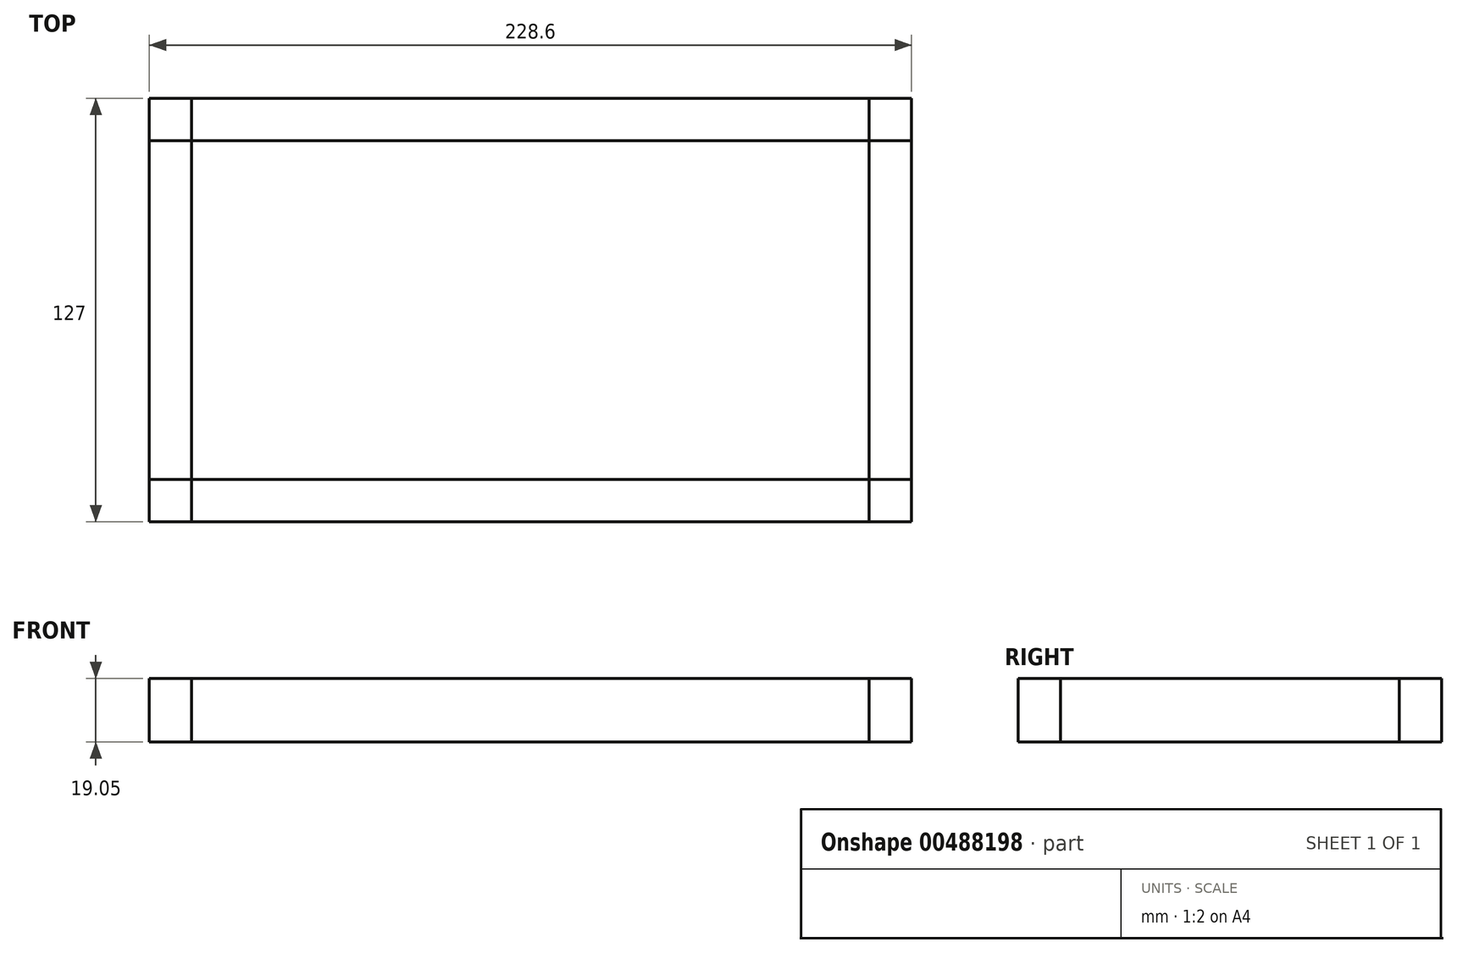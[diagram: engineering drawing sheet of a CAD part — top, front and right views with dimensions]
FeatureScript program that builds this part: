
annotation { "Feature Type Name" : "Feature", "Feature Type Description" : "" }
export const myFeature = defineFeature(function(context is Context, id is Id, definition is map)
    precondition{}
    {
        {
            var Q0;
            Q0=qCreatedBy(makeId("Top.planeOp"),FACE);
            var sketch = newSketch(context, id + "F0", { "sketchPlane" : qUnion([Q0])});
            skLineSegment(sketch, "E0.bottom", {"start": v(101.6, -50.8) * mm, "end": v(-101.6, -50.8) * mm});
            skLineSegment(sketch, "E0.top", {"start": v(101.6, 50.8) * mm, "end": v(-101.6, 50.8) * mm});
            skLineSegment(sketch, "E0.left", {"start": v(101.6, -50.8) * mm, "end": v(101.6, 50.8) * mm});
            skLineSegment(sketch, "E0.right", {"start": v(-101.6, -50.8) * mm, "end": v(-101.6, 50.8) * mm});
            skPoint(sketch, "E0.middle", {"position": v(0, 0) * mm});
            skSolve(sketch);
        }
        {
            var Q0;
            Q0=makeQuery(id+"F0.imprint","IMPRINT",FACE,{"disambiguationData":[TD([[makeQuery(id+"F0.imprint","IMPRINT",EDGE,{"derivedFrom":sQuery(id+"F0.wireOp",EDGE,"E0.bottom")}),-1.0]])]});
            extrude(context, id + "F1", {"entities" : qUnion([Q0]), "depth" : 19.05 * mm});
        }
        {
            var Q0;
            Q0=makeQuery(id+"F1.opExtrude","CAP_FACE",FACE,{"disambiguationData":[OSD([sQuery(id+"F0.wireOp",EDGE,"E0.bottom"),sQuery(id+"F0.wireOp",EDGE,"E0.top"),sQuery(id+"F0.wireOp",EDGE,"E0.left"),sQuery(id+"F0.wireOp",EDGE,"E0.right")])],"isStart":false});
            var sketch = newSketch(context, id + "F2", { "sketchPlane" : qUnion([Q0])});
            skLineSegment(sketch, "E1.bottom", {"start": v(-101.6, -50.8) * mm, "end": v(-114.3, -50.8) * mm});
            skLineSegment(sketch, "E1.top", {"start": v(-101.6, -63.5) * mm, "end": v(-114.3, -63.5) * mm});
            skLineSegment(sketch, "E1.left", {"start": v(-101.6, -50.8) * mm, "end": v(-101.6, -63.5) * mm});
            skLineSegment(sketch, "E1.right", {"start": v(-114.3, -50.8) * mm, "end": v(-114.3, -63.5) * mm});
            skSolve(sketch);
        }
        {
            var Q0;
            Q0=makeQuery(id+"F2.imprint","IMPRINT",FACE,{"disambiguationData":[TD([[makeQuery(id+"F2.imprint","IMPRINT",EDGE,{"derivedFrom":sQuery(id+"F2.wireOp",EDGE,"E1.bottom")}),1.0]])]});
            extrude(context, id + "F3", {"entities" : qUnion([Q0]), "oppositeDirection" : true, "depth" : 19.05 * mm});
        }
        {
            var Q0;
            Q0=makeQuery(id+"F3.opExtrude","SWEPT_BODY",BODY,{"disambiguationData":[OSD([sQuery(id+"F2.wireOp",EDGE,"E1.bottom"),sQuery(id+"F2.wireOp",EDGE,"E1.top"),sQuery(id+"F2.wireOp",EDGE,"E1.left"),sQuery(id+"F2.wireOp",EDGE,"E1.right")])]});
            var Q1;
            Q1=qCreatedBy(makeId("Right.planeOp"),FACE);
            mirror(context, id + "F4", {"entities" : qUnion([Q0]), "mirrorPlane" : qUnion([Q1])});
        }
        {
            var Q0;
            Q0=makeQuery(id+"F3.opExtrude","SWEPT_BODY",BODY,{"disambiguationData":[OSD([sQuery(id+"F2.wireOp",EDGE,"E1.bottom"),sQuery(id+"F2.wireOp",EDGE,"E1.top"),sQuery(id+"F2.wireOp",EDGE,"E1.left"),sQuery(id+"F2.wireOp",EDGE,"E1.right")])]});
            var Q1;
            Q1=makeQuery(id+"F4.opPattern","COPY",BODY,{"derivedFrom":makeQuery(id+"F3.opExtrude","SWEPT_BODY",BODY,{"disambiguationData":[OSD([sQuery(id+"F2.wireOp",EDGE,"E1.bottom"),sQuery(id+"F2.wireOp",EDGE,"E1.top"),sQuery(id+"F2.wireOp",EDGE,"E1.left"),sQuery(id+"F2.wireOp",EDGE,"E1.right")])]}),"instanceName":"1"});
            var Q2;
            Q2=qCreatedBy(makeId("Front.planeOp"),FACE);
            mirror(context, id + "F5", {"entities" : qUnion([Q0, Q1]), "mirrorPlane" : qUnion([Q2])});
        }
        {
            var Q0;
            Q0=makeQuery(id+"F1.opExtrude","CAP_FACE",FACE,{"disambiguationData":[OSD([sQuery(id+"F0.wireOp",EDGE,"E0.bottom"),sQuery(id+"F0.wireOp",EDGE,"E0.top"),sQuery(id+"F0.wireOp",EDGE,"E0.left"),sQuery(id+"F0.wireOp",EDGE,"E0.right")])],"isStart":false});
            var sketch = newSketch(context, id + "F6", { "sketchPlane" : qUnion([Q0])});
            skPoint(sketch, "E2.0", {"position": v(101.6, -63.5) * mm});
            skPoint(sketch, "E3.0", {"position": v(-101.6, -63.5) * mm});
            skLineSegment(sketch, "E4.bottom", {"start": v(-101.6, -63.5) * mm, "end": v(101.6, -63.5) * mm});
            skLineSegment(sketch, "E4.top", {"start": v(-101.6, -50.8) * mm, "end": v(101.6, -50.8) * mm});
            skLineSegment(sketch, "E4.left", {"start": v(-101.6, -63.5) * mm, "end": v(-101.6, -50.8) * mm});
            skLineSegment(sketch, "E4.right", {"start": v(101.6, -63.5) * mm, "end": v(101.6, -50.8) * mm});
            skSolve(sketch);
        }
        {
            var Q0;
            Q0=makeQuery(id+"F6.imprint","IMPRINT",FACE,{"disambiguationData":[TD([[makeQuery(id+"F6.imprint","IMPRINT",EDGE,{"derivedFrom":sQuery(id+"F6.wireOp",EDGE,"E4.bottom")}),1.0]])]});
            extrude(context, id + "F7", {"entities" : qUnion([Q0]), "oppositeDirection" : true, "depth" : 19.05 * mm});
        }
        {
            var Q0;
            Q0=makeQuery(id+"F7.opExtrude","SWEPT_BODY",BODY,{"disambiguationData":[OSD([sQuery(id+"F6.wireOp",EDGE,"E4.bottom"),sQuery(id+"F6.wireOp",EDGE,"E4.top"),sQuery(id+"F6.wireOp",EDGE,"E4.left"),sQuery(id+"F6.wireOp",EDGE,"E4.right")])]});
            var Q1;
            Q1=qCreatedBy(makeId("Front.planeOp"),FACE);
            mirror(context, id + "F8", {"entities" : qUnion([Q0]), "mirrorPlane" : qUnion([Q1])});
        }
        {
            var Q0;
            Q0=makeQuery(id+"F1.opExtrude","CAP_FACE",FACE,{"disambiguationData":[OSD([sQuery(id+"F0.wireOp",EDGE,"E0.bottom"),sQuery(id+"F0.wireOp",EDGE,"E0.top"),sQuery(id+"F0.wireOp",EDGE,"E0.left"),sQuery(id+"F0.wireOp",EDGE,"E0.right")])],"isStart":false});
            var sketch = newSketch(context, id + "F9", { "sketchPlane" : qUnion([Q0])});
            skPoint(sketch, "E5.0", {"position": v(-114.3, -50.8) * mm});
            skLineSegment(sketch, "E6.bottom", {"start": v(-101.6, 50.8) * mm, "end": v(-114.3, 50.8) * mm});
            skLineSegment(sketch, "E6.top", {"start": v(-101.6, -50.8) * mm, "end": v(-114.3, -50.8) * mm});
            skLineSegment(sketch, "E6.left", {"start": v(-101.6, 50.8) * mm, "end": v(-101.6, -50.8) * mm});
            skLineSegment(sketch, "E6.right", {"start": v(-114.3, 50.8) * mm, "end": v(-114.3, -50.8) * mm});
            skSolve(sketch);
        }
        {
            var Q0;
            Q0 = qSketchRegion(id + "F9", true);
            extrude(context, id + "F10", {"entities" : qUnion([Q0]), "oppositeDirection" : true, "depth" : 3 / 101.6 * mm});
        }
        {
            var Q0;
            Q0=makeQuery(id+"F10.opExtrude","SWEPT_BODY",BODY,{"disambiguationData":[OSD([sQuery(id+"F9.wireOp",EDGE,"E6.bottom"),sQuery(id+"F9.wireOp",EDGE,"E6.top"),sQuery(id+"F9.wireOp",EDGE,"E6.left"),sQuery(id+"F9.wireOp",EDGE,"E6.right")])]});
            var Q1;
            Q1=qCreatedBy(makeId("Right.planeOp"),FACE);
            mirror(context, id + "F11", {"entities" : qUnion([Q0]), "mirrorPlane" : qUnion([Q1])});
        }
    });
